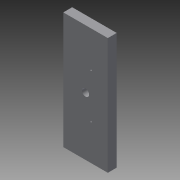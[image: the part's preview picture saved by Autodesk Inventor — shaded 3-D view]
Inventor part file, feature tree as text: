
AUTODESK INVENTOR PART (.ipt)
format: ipt  version: 2015 (Build 190159000, 159)  size: 82,944 bytes
history: native  units: mm
features: extrude x3, sketch x2
ambient origin geometry x8: Origin, YZ Plane, XZ Plane, XY Plane, X Axis, Y Axis, Z Axis, Center Point
bodies: Solid1 (feature_tree)
feature tree (5):
  sketch  "Sketch1"  dims[d0=50.0mm d1=131.0mm]
  extrude  "Extrusion1"  Depth=131.0mm
  extrude  "Extrusion2"  Depth=10.0mm
  extrude  "Extrusion3"  Depth=10.0mm
  sketch  "Sketch2"  dims[d2=10.0mm d3=0.0mm d4=8.0mm d10=2.0mm d11=10.0mm d12=0.0mm d14=2.5mm d15=10.0mm d16=0.0mm]
